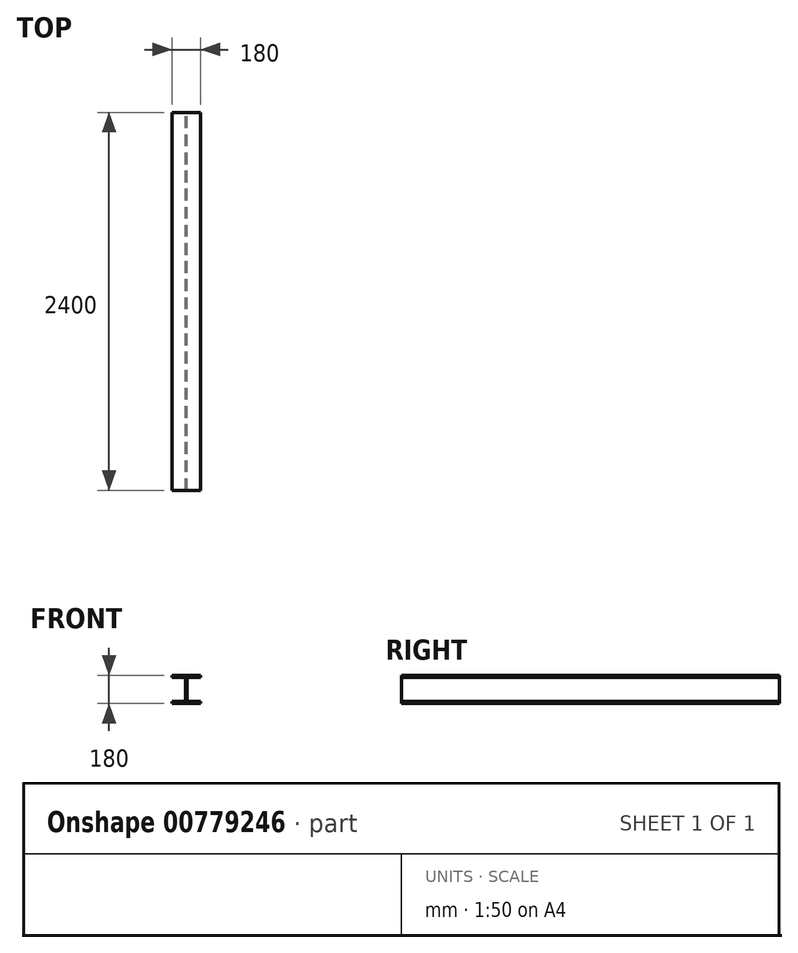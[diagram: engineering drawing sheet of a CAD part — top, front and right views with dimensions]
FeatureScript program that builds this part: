
annotation { "Feature Type Name" : "Feature", "Feature Type Description" : "" }
export const myFeature = defineFeature(function(context is Context, id is Id, definition is map)
    precondition{}
    {
        {
            var Q0;
            Q0=qCreatedBy(makeId("Front.planeOp"),FACE);
            var sketch = newSketch(context, id + "F0", { "sketchPlane" : qUnion([Q0])});
            skLineSegment(sketch, "E0.bottom", {"start": v(0, 0) * mm, "end": v(180, 0) * mm});
            skLineSegment(sketch, "E0.top", {"start": v(0, 180) * mm, "end": v(180, 180) * mm});
            skLineSegment(sketch, "E0.left", {"start": v(0, 0) * mm, "end": v(0, 14) * mm});
            skLineSegment(sketch, "E0.right", {"start": v(180, 0) * mm, "end": v(180, 14) * mm});
            skLineSegment(sketch, "E1.bottom", {"start": v(180, 166) * mm, "end": v(109.25, 166) * mm});
            skLineSegment(sketch, "E1.top", {"start": v(180, 14) * mm, "end": v(109.25, 14) * mm});
            skLineSegment(sketch, "E1.right", {"start": v(94.25, 151) * mm, "end": v(94.25, 29) * mm});
            skLineSegment(sketch, "E2.bottom", {"start": v(0, 166) * mm, "end": v(70.75, 166) * mm});
            skLineSegment(sketch, "E2.top", {"start": v(0, 14) * mm, "end": v(70.75, 14) * mm});
            skLineSegment(sketch, "E2.right", {"start": v(85.75, 151) * mm, "end": v(85.75, 29) * mm});
            skLineSegment(sketch, "E3.trimOffspring", {"start": v(0, 166) * mm, "end": v(0, 180) * mm});
            skLineSegment(sketch, "E4.trimOffspring", {"start": v(180, 166) * mm, "end": v(180, 180) * mm});
            skPoint(sketch, "E5.visualSharp", {"position": v(94.25, 166) * mm});
            skArc(sketch, "E5.filletArc", {"start": v(109.25, 166) * mm, "mid": v(98.64, 161.6) * mm, "end": v(94.25, 151) * mm});
            skPoint(sketch, "E6.visualSharp", {"position": v(85.75, 166) * mm});
            skArc(sketch, "E6.filletArc", {"start": v(85.75, 151) * mm, "mid": v(81.36, 161.6) * mm, "end": v(70.75, 166) * mm});
            skPoint(sketch, "E7.visualSharp", {"position": v(94.25, 14) * mm});
            skArc(sketch, "E7.filletArc", {"start": v(94.25, 29) * mm, "mid": v(98.64, 18.4) * mm, "end": v(109.25, 14) * mm});
            skPoint(sketch, "E8.visualSharp", {"position": v(85.75, 14) * mm});
            skArc(sketch, "E8.filletArc", {"start": v(70.75, 14) * mm, "mid": v(81.36, 18.4) * mm, "end": v(85.75, 29) * mm});
            skSolve(sketch);
        }
        {
            var Q0;
            Q0=makeQuery(id+"F0.imprint","IMPRINT",FACE,{"disambiguationData":[TD([[makeQuery(id+"F0.imprint","IMPRINT",EDGE,{"derivedFrom":sQuery(id+"F0.wireOp",EDGE,"E0.bottom")}),1.0]])]});
            extrude(context, id + "F1", {"entities" : qUnion([Q0]), "endBound" : BoundingType.SYMMETRIC, "depth" : 2400 * mm, "offsetDistance" : 25 * mm});
        }
    });
